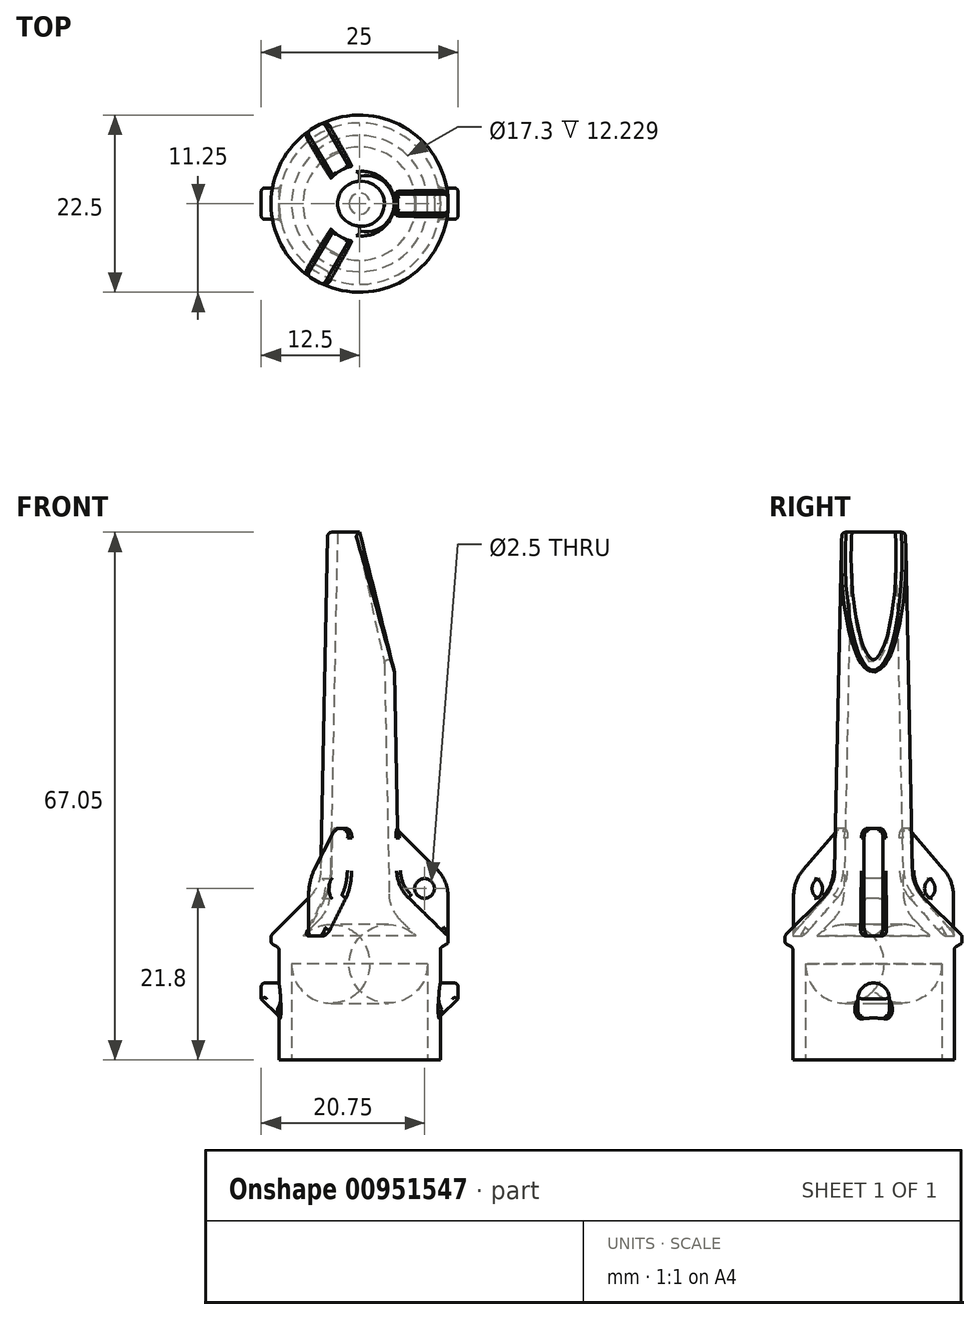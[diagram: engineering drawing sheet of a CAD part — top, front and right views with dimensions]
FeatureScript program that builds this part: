
annotation { "Feature Type Name" : "Feature", "Feature Type Description" : "" }
export const myFeature = defineFeature(function(context is Context, id is Id, definition is map)
    precondition{}
    {
        {
            var Q0;
            Q0=qCreatedBy(makeId("Front.planeOp"),FACE);
            var sketch = newSketch(context, id + "F0", { "sketchPlane" : qUnion([Q0])});
            skLineSegment(sketch, "E0", {"start": v(0, 0) * mm, "end": v(4.05, 0) * mm});
            skLineSegment(sketch, "E1", {"start": v(4.05, 0) * mm, "end": v(5, 45) * mm});
            skLineSegment(sketch, "E2", {"start": v(5, 45) * mm, "end": v(11.25, 51.25) * mm});
            skLineSegment(sketch, "E3", {"start": v(11.25, 51.25) * mm, "end": v(11.25, 52.75) * mm});
            skLineSegment(sketch, "E4", {"start": v(11.25, 52.75) * mm, "end": v(10.25, 52.75) * mm});
            skLineSegment(sketch, "E5", {"start": v(10.25, 52.75) * mm, "end": v(10.25, 67.05) * mm});
            skLineSegment(sketch, "E6", {"start": v(10.25, 67.05) * mm, "end": v(0, 67.05) * mm});
            skLineSegment(sketch, "E7", {"start": v(0, 67.05) * mm, "end": v(0, 0) * mm});
            skSolve(sketch);
        }
        {
            var Q0;
            Q0=qCreatedBy(makeId("Front.planeOp"),FACE);
            var sketch = newSketch(context, id + "F1", { "sketchPlane" : qUnion([Q0])});
            skLineSegment(sketch, "E8", {"start": v(0, 67.05) * mm, "end": v(8.65, 67.05) * mm});
            skLineSegment(sketch, "E9", {"start": v(8.65, 67.05) * mm, "end": v(8.65, 52.75) * mm});
            skLineSegment(sketch, "E10", {"start": v(8.65, 52.75) * mm, "end": v(3.81, 47.91) * mm});
            skLineSegment(sketch, "E11", {"start": v(3.81, 47.91) * mm, "end": v(2.8, 0) * mm});
            skLineSegment(sketch, "E12", {"start": v(2.8, 0) * mm, "end": v(0, 0) * mm});
            skLineSegment(sketch, "E13", {"start": v(0, 0) * mm, "end": v(0, 67.05) * mm});
            skSolve(sketch);
        }
        {
            var Q0;
            Q0=qSketchRegion(id+"F0",true);
            var Q1;
            Q1=sQuery(id+"F0.wireOp",EDGE,"E7");
            revolve(context, id + "F2", {"surfaceOperationType" : NewSurfaceOperationType.NEW, "entities" : qUnion([Q0]), "axis" : qUnion([Q1]), "revolveType" : RevolveType.FULL});
        }
        {
            var Q0;
            Q0=makeQuery(id+"F2.opRevolve","SWEPT_EDGE",EDGE,{"disambiguationData":[OSD([sQuery(id+"F0.wireOp",EDGE,"E1"),sQuery(id+"F0.wireOp",EDGE,"E2")])]});
            fillet(context, id + "F3", {"entities" : qUnion([Q0]), "radius" : 5 * mm, "tangentPropagation" : true, "allowEdgeOverflow" : false});
        }
        {
            var Q0;
            Q0=makeQuery(id+"F2.opRevolve","SWEPT_EDGE",EDGE,{"disambiguationData":[OSD([sQuery(id+"F0.wireOp",EDGE,"E2"),sQuery(id+"F0.wireOp",EDGE,"E3")])]});
            fillet(context, id + "F4", {"entities" : qUnion([Q0]), "radius" : 0.5 * mm, "tangentPropagation" : true, "allowEdgeOverflow" : false});
        }
        {
            var Q0;
            Q0=qCreatedBy(makeId("Front.planeOp"),FACE);
            var sketch = newSketch(context, id + "F5", { "sketchPlane" : qUnion([Q0])});
            skLineSegment(sketch, "E14", {"start": v(0, 51.25) * mm, "end": v(11.25, 51.25) * mm});
            skLineSegment(sketch, "E15", {"start": v(11.25, 51.25) * mm, "end": v(11.25, 44.25) * mm});
            skLineSegment(sketch, "E16", {"start": v(11.25, 44.25) * mm, "end": v(0, 33) * mm});
            skLineSegment(sketch, "E17", {"start": v(0, 33) * mm, "end": v(0, 51.25) * mm});
            skLineSegment(sketch, "E18", {"start": v(8.25, 44.25) * mm, "end": v(11.25, 44.25) * mm, "construction": true});
            skLineSegment(sketch, "E19", {"start": v(8.25, 44.25) * mm, "end": v(8.25, 45.25) * mm, "construction": true});
            skCircle(sketch, "E20", {"center": v(8.25, 45.25) * mm, "radius": 1.25 * mm});
            skSolve(sketch);
        }
        {
            var Q0;
            Q0=qSketchRegion(id+"F5",true);
            extrude(context, id + "F6", {"entities" : qUnion([Q0]), "endBound" : BoundingType.SYMMETRIC, "depth" : 2.4 * mm, "offsetDistance" : 25 * mm});
        }
        {
            var Q0;
            Q0=makeQuery(id+"F6.opExtrude","SWEPT_EDGE",EDGE,{"disambiguationData":[OSD([sQuery(id+"F5.wireOp",EDGE,"E15"),sQuery(id+"F5.wireOp",EDGE,"E16")])]});
            fillet(context, id + "F7", {"entities" : qUnion([Q0]), "radius" : 5 * mm, "tangentPropagation" : true, "allowEdgeOverflow" : false});
        }
        {
            var Q0;
            Q0=makeQuery(id+"F6.opExtrude","CAP_EDGE",EDGE,{"disambiguationData":[OSD([sQuery(id+"F5.wireOp",EDGE,"E15")])],"isStart":false});
            var Q1;
            {var subQ0=sQuery(id+"F5.wireOp",EDGE,"E16");var subQ1=sQuery(id+"F5.wireOp",EDGE,"E15");Q1=makeQuery(id+"F7.opFillet","BLEND_EDGE",EDGE,{"blendedFrom":[makeQuery(id+"F6.opExtrude","SWEPT_EDGE",EDGE,{"disambiguationData":[OSD([subQ1,subQ0])]}),makeQuery(id+"F6.opExtrude","CAP_FACE",FACE,{"disambiguationData":[OSD([sQuery(id+"F5.wireOp",EDGE,"E14"),subQ1,subQ0,sQuery(id+"F5.wireOp",EDGE,"E17")])],"isStart":true})],"blendedInto":[makeQuery(id+"F6.opExtrude","CAP_FACE",FACE,{"disambiguationData":[OSD([sQuery(id+"F5.wireOp",EDGE,"E14"),subQ1,subQ0,sQuery(id+"F5.wireOp",EDGE,"E17")])],"isStart":true})]});}
            fillet(context, id + "F8", {"entities" : qUnion([Q0, Q1]), "radius" : 0.5 * mm, "tangentPropagation" : true, "allowEdgeOverflow" : false});
        }
        {
            var Q0;
            Q0=makeQuery(id+"F6.opExtrude","SWEPT_BODY",BODY,{"disambiguationData":[OSD([sQuery(id+"F5.wireOp",EDGE,"E14"),sQuery(id+"F5.wireOp",EDGE,"E15"),sQuery(id+"F5.wireOp",EDGE,"E16"),sQuery(id+"F5.wireOp",EDGE,"E17")])]});
            var Q1;
            Q1=sQuery(id+"F0.wireOp",EDGE,"E7");
            circularPattern(context, id + "F9", {"operationType" : NewBodyOperationType.ADD, "entities" : qUnion([Q0]), "axis" : qUnion([Q1]), "angle" : 240 * degree, "instanceCount" : 3, "equalSpace" : true});
        }
        {
            var Q0;
            Q0=makeQuery(id+"F9.boolean.opBoolean","INTERSECT",EDGE,{"derivedFrom":[makeQuery(id+"F2.opRevolve","SWEPT_FACE",FACE,{"disambiguationData":[OSD([sQuery(id+"F0.wireOp",EDGE,"E2")])]}),makeQuery(id+"F9.opPattern","COPY",FACE,{"derivedFrom":makeQuery(id+"F6.opExtrude","CAP_FACE",FACE,{"disambiguationData":[OSD([sQuery(id+"F5.wireOp",EDGE,"E14"),sQuery(id+"F5.wireOp",EDGE,"E15"),sQuery(id+"F5.wireOp",EDGE,"E16"),sQuery(id+"F5.wireOp",EDGE,"E17")])],"isStart":false}),"instanceName":"1"})]});
            var Q1;
            Q1=makeQuery(id+"F9.boolean.opBoolean","INTERSECT",EDGE,{"derivedFrom":[makeQuery(id+"F2.opRevolve","SWEPT_FACE",FACE,{"disambiguationData":[OSD([sQuery(id+"F0.wireOp",EDGE,"E2")])]}),makeQuery(id+"F9.opPattern","COPY",FACE,{"derivedFrom":makeQuery(id+"F6.opExtrude","CAP_FACE",FACE,{"disambiguationData":[OSD([sQuery(id+"F5.wireOp",EDGE,"E14"),sQuery(id+"F5.wireOp",EDGE,"E15"),sQuery(id+"F5.wireOp",EDGE,"E16"),sQuery(id+"F5.wireOp",EDGE,"E17")])],"isStart":true}),"instanceName":"2"})]});
            var Q2;
            Q2=makeQuery(id+"F9.boolean.opBoolean","INTERSECT",EDGE,{"derivedFrom":[makeQuery(id+"F2.opRevolve","SWEPT_FACE",FACE,{"disambiguationData":[OSD([sQuery(id+"F0.wireOp",EDGE,"E2")])]}),makeQuery(id+"F6.opExtrude","CAP_FACE",FACE,{"disambiguationData":[OSD([sQuery(id+"F5.wireOp",EDGE,"E14"),sQuery(id+"F5.wireOp",EDGE,"E15"),sQuery(id+"F5.wireOp",EDGE,"E16"),sQuery(id+"F5.wireOp",EDGE,"E17")])],"isStart":false})]});
            var Q3;
            Q3=makeQuery(id+"F6.opExtrude","CAP_EDGE",EDGE,{"disambiguationData":[OSD([sQuery(id+"F5.wireOp",EDGE,"E20")])],"isStart":false});
            var Q4;
            Q4=makeQuery(id+"F6.opExtrude","CAP_EDGE",EDGE,{"disambiguationData":[OSD([sQuery(id+"F5.wireOp",EDGE,"E20")])],"isStart":true});
            var Q5;
            Q5=makeQuery(id+"F9.opPattern","COPY",EDGE,{"derivedFrom":makeQuery(id+"F6.opExtrude","CAP_EDGE",EDGE,{"disambiguationData":[OSD([sQuery(id+"F5.wireOp",EDGE,"E20")])],"isStart":true}),"instanceName":"1"});
            var Q6;
            Q6=makeQuery(id+"F9.opPattern","COPY",EDGE,{"derivedFrom":makeQuery(id+"F6.opExtrude","CAP_EDGE",EDGE,{"disambiguationData":[OSD([sQuery(id+"F5.wireOp",EDGE,"E20")])],"isStart":false}),"instanceName":"2"});
            var Q7;
            Q7=makeQuery(id+"F9.opPattern","COPY",EDGE,{"derivedFrom":makeQuery(id+"F6.opExtrude","CAP_EDGE",EDGE,{"disambiguationData":[OSD([sQuery(id+"F5.wireOp",EDGE,"E20")])],"isStart":true}),"instanceName":"2"});
            var Q8;
            Q8=makeQuery(id+"F9.opPattern","COPY",EDGE,{"derivedFrom":makeQuery(id+"F6.opExtrude","CAP_EDGE",EDGE,{"disambiguationData":[OSD([sQuery(id+"F5.wireOp",EDGE,"E20")])],"isStart":false}),"instanceName":"1"});
            fillet(context, id + "F10", {"entities" : qUnion([Q0, Q1, Q2, Q3, Q4, Q5, Q6, Q7, Q8]), "radius" : 0.5 * mm, "tangentPropagation" : true, "allowEdgeOverflow" : false});
        }
        {
            var Q0;
            Q0=makeQuery(id+"F2.opRevolve","SWEPT_EDGE",EDGE,{"disambiguationData":[OSD([sQuery(id+"F0.wireOp",EDGE,"E3"),sQuery(id+"F0.wireOp",EDGE,"E4")])]});
            chamfer(context, id + "F11", {"entities" : qUnion([Q0]), "chamferType" : ChamferType.TWO_OFFSETS, "width1" : 0.5 * mm, "oppositeDirection" : true, "width2" : 1 * mm, "tangentPropagation" : true});
        }
        {
            var Q0;
            Q0=qCreatedBy(makeId("Front.planeOp"),FACE);
            var sketch = newSketch(context, id + "F12", { "sketchPlane" : qUnion([Q0])});
            skLineSegment(sketch, "E21", {"start": v(0, 57.25) * mm, "end": v(12.5, 57.25) * mm});
            skLineSegment(sketch, "E22", {"start": v(12.5, 57.25) * mm, "end": v(12.5, 59.25) * mm});
            skLineSegment(sketch, "E23", {"start": v(12.5, 59.25) * mm, "end": v(6.5, 65.25) * mm});
            skLineSegment(sketch, "E24", {"start": v(6.5, 65.25) * mm, "end": v(0, 65.25) * mm});
            skLineSegment(sketch, "E25", {"start": v(0, 65.25) * mm, "end": v(0, 57.25) * mm});
            skSolve(sketch);
        }
        {
            var Q0;
            Q0 = qSketchRegion(id + "F12", true);
            extrude(context, id + "F13", {"entities" : qUnion([Q0]), "endBound" : BoundingType.SYMMETRIC, "depth" : 4 * mm, "offsetDistance" : 25 * mm});
        }
        {
            var Q0;
            Q0=makeQuery(id+"F13.opExtrude","CAP_EDGE",EDGE,{"disambiguationData":[OSD([sQuery(id+"F12.wireOp",EDGE,"E21")])],"isStart":false});
            var Q1;
            Q1=makeQuery(id+"F13.opExtrude","CAP_EDGE",EDGE,{"disambiguationData":[OSD([sQuery(id+"F12.wireOp",EDGE,"E21")])],"isStart":true});
            fillet(context, id + "F14", {"entities" : qUnion([Q0, Q1]), "radius" : 2 * mm, "tangentPropagation" : true, "allowEdgeOverflow" : false});
        }
        {
            var Q0;
            Q0=makeQuery(id+"F13.opExtrude","SWEPT_BODY",BODY,{"disambiguationData":[OSD([sQuery(id+"F12.wireOp",EDGE,"E21"),sQuery(id+"F12.wireOp",EDGE,"E22"),sQuery(id+"F12.wireOp",EDGE,"E23"),sQuery(id+"F12.wireOp",EDGE,"E24"),sQuery(id+"F12.wireOp",EDGE,"E25")])]});
            var Q1;
            Q1=sQuery(id+"F1.wireOp",EDGE,"E13");
            circularPattern(context, id + "F15", {"operationType" : NewBodyOperationType.ADD, "entities" : qUnion([Q0]), "axis" : qUnion([Q1]), "angle" : 360 * degree, "instanceCount" : 2, "equalSpace" : true});
        }
        {
            var Q0;
            Q0=makeQuery(id+"F13.opExtrude","CAP_EDGE",EDGE,{"disambiguationData":[OSD([sQuery(id+"F12.wireOp",EDGE,"E23")])],"isStart":true});
            var Q1;
            Q1=makeQuery(id+"F13.opExtrude","CAP_EDGE",EDGE,{"disambiguationData":[OSD([sQuery(id+"F12.wireOp",EDGE,"E23")])],"isStart":false});
            var Q2;
            Q2=makeQuery(id+"F14.opFillet","BLEND_EDGE",EDGE,{"blendedFrom":[makeQuery(id+"F13.opExtrude","CAP_EDGE",EDGE,{"disambiguationData":[OSD([sQuery(id+"F12.wireOp",EDGE,"E21")])],"isStart":true}),makeQuery(id+"F13.opExtrude","SWEPT_FACE",FACE,{"disambiguationData":[OSD([sQuery(id+"F12.wireOp",EDGE,"E22")])]})],"blendedInto":[makeQuery(id+"F13.opExtrude","SWEPT_FACE",FACE,{"disambiguationData":[OSD([sQuery(id+"F12.wireOp",EDGE,"E22")])]})]});
            var Q3;
            Q3=makeQuery(id+"F15.boolean.opBoolean","INTERSECT",EDGE,{"derivedFrom":[makeQuery(id+"F2.opRevolve","SWEPT_FACE",FACE,{"disambiguationData":[OSD([sQuery(id+"F0.wireOp",EDGE,"E5")])]}),makeQuery(id+"F13.opExtrude","SWEPT_FACE",FACE,{"disambiguationData":[OSD([sQuery(id+"F12.wireOp",EDGE,"E23")])]})]});
            var Q4;
            Q4=makeQuery(id+"F15.opPattern","COPY",EDGE,{"derivedFrom":makeQuery(id+"F13.opExtrude","CAP_EDGE",EDGE,{"disambiguationData":[OSD([sQuery(id+"F12.wireOp",EDGE,"E23")])],"isStart":false}),"instanceName":"1"});
            var Q5;
            Q5=makeQuery(id+"F15.opPattern","COPY",EDGE,{"derivedFrom":makeQuery(id+"F13.opExtrude","CAP_EDGE",EDGE,{"disambiguationData":[OSD([sQuery(id+"F12.wireOp",EDGE,"E23")])],"isStart":true}),"instanceName":"1"});
            var Q6;
            Q6=makeQuery(id+"F15.boolean.opBoolean","INTERSECT",EDGE,{"derivedFrom":[makeQuery(id+"F2.opRevolve","SWEPT_FACE",FACE,{"disambiguationData":[OSD([sQuery(id+"F0.wireOp",EDGE,"E5")])]}),makeQuery(id+"F15.opPattern","COPY",FACE,{"derivedFrom":makeQuery(id+"F13.opExtrude","SWEPT_FACE",FACE,{"disambiguationData":[OSD([sQuery(id+"F12.wireOp",EDGE,"E23")])]}),"instanceName":"1"})]});
            var Q7;
            Q7=makeQuery(id+"F15.opPattern","COPY",EDGE,{"derivedFrom":makeQuery(id+"F14.opFillet","BLEND_EDGE",EDGE,{"blendedFrom":[makeQuery(id+"F13.opExtrude","CAP_EDGE",EDGE,{"disambiguationData":[OSD([sQuery(id+"F12.wireOp",EDGE,"E21")])],"isStart":true}),makeQuery(id+"F13.opExtrude","SWEPT_FACE",FACE,{"disambiguationData":[OSD([sQuery(id+"F12.wireOp",EDGE,"E22")])]})],"blendedInto":[makeQuery(id+"F13.opExtrude","SWEPT_FACE",FACE,{"disambiguationData":[OSD([sQuery(id+"F12.wireOp",EDGE,"E22")])]})]}),"instanceName":"1"});
            fillet(context, id + "F16", {"entities" : qUnion([Q0, Q1, Q2, Q3, Q4, Q5, Q6, Q7]), "radius" : 0.5 * mm, "tangentPropagation" : true, "allowEdgeOverflow" : false});
        }
        {
            var Q0;
            Q0=qSketchRegion(id+"F1",true);
            var Q1;
            Q1=sQuery(id+"F1.wireOp",EDGE,"E13");
            revolve(context, id + "F17", {"operationType" : NewBodyOperationType.REMOVE, "surfaceOperationType" : NewSurfaceOperationType.NEW, "entities" : qUnion([Q0]), "axis" : qUnion([Q1]), "revolveType" : RevolveType.FULL, "oppositeDirection" : true});
        }
        {
            var Q0;
            Q0=makeQuery(id+"F17.boolean.opBoolean","COPY",EDGE,{"derivedFrom":makeQuery(id+"F17.opRevolve","SWEPT_EDGE",EDGE,{"disambiguationData":[OSD([sQuery(id+"F1.wireOp",EDGE,"E10"),sQuery(id+"F1.wireOp",EDGE,"E11")])]})});
            var Q1;
            Q1=makeQuery(id+"F17.boolean.opBoolean","COPY",EDGE,{"derivedFrom":makeQuery(id+"F17.opRevolve","SWEPT_EDGE",EDGE,{"disambiguationData":[OSD([sQuery(id+"F1.wireOp",EDGE,"E9"),sQuery(id+"F1.wireOp",EDGE,"E10")])]})});
            fillet(context, id + "F18", {"entities" : qUnion([Q0, Q1]), "radius" : 5 * mm, "tangentPropagation" : true, "allowEdgeOverflow" : false});
        }
        {
            var Q0;
            {var subQ0=sQuery(id+"F0.wireOp",EDGE,"E3");Q0=makeQuery(id+"F11.opChamfer","BLEND_EDGE",EDGE,{"blendedFrom":[makeQuery(id+"F2.opRevolve","SWEPT_EDGE",EDGE,{"disambiguationData":[OSD([subQ0,sQuery(id+"F0.wireOp",EDGE,"E4")])]}),makeQuery(id+"F2.opRevolve","SWEPT_FACE",FACE,{"disambiguationData":[OSD([subQ0])]})],"blendedInto":[makeQuery(id+"F2.opRevolve","SWEPT_FACE",FACE,{"disambiguationData":[OSD([subQ0])]})]});}
            var Q1;
            Q1=makeQuery(id+"F11.opChamfer","BLEND_EDGE",EDGE,{"blendedFrom":[makeQuery(id+"F2.opRevolve","SWEPT_EDGE",EDGE,{"disambiguationData":[OSD([sQuery(id+"F0.wireOp",EDGE,"E3"),sQuery(id+"F0.wireOp",EDGE,"E4")])]}),makeQuery(id+"F2.opRevolve","SWEPT_FACE",FACE,{"disambiguationData":[OSD([sQuery(id+"F0.wireOp",EDGE,"E5")])]})],"blendedInto":[makeQuery(id+"F2.opRevolve","SWEPT_FACE",FACE,{"disambiguationData":[OSD([sQuery(id+"F0.wireOp",EDGE,"E5")])]})]});
            fillet(context, id + "F19", {"entities" : qUnion([Q0, Q1]), "radius" : 0.5 * mm, "tangentPropagation" : true, "allowEdgeOverflow" : false});
        }
        {
            var Q0;
            Q0=qCreatedBy(makeId("Front.planeOp"),FACE);
            var sketch = newSketch(context, id + "F20", { "sketchPlane" : qUnion([Q0])});
            skLineSegment(sketch, "E26", {"start": v(0, 0) * mm, "end": v(5, 20) * mm});
            skLineSegment(sketch, "E27", {"start": v(5, 20) * mm, "end": v(5, 0) * mm});
            skLineSegment(sketch, "E28", {"start": v(5, 0) * mm, "end": v(0, 0) * mm});
            skSolve(sketch);
        }
        {
            var Q0;
            Q0 = qSketchRegion(id + "F20", true);
            extrude(context, id + "F21", {"entities" : qUnion([Q0]), "operationType" : NewBodyOperationType.REMOVE, "endBound" : BoundingType.SYMMETRIC, "oppositeDirection" : true, "depth" : 25 * mm, "offsetDistance" : 25 * mm});
        }
        {
            var Q0;
            Q0=makeQuery(id+"F2.opRevolve","SWEPT_EDGE",EDGE,{"disambiguationData":[OSD([sQuery(id+"F0.wireOp",EDGE,"E0"),sQuery(id+"F0.wireOp",EDGE,"E1")])]});
            var Q1;
            Q1=makeQuery(id+"F21.boolean.opBoolean","COPY",EDGE,{"disambiguationData":[OD(0.0)],"derivedFrom":makeQuery(id+"F21.opExtrude","SWEPT_EDGE",EDGE,{"disambiguationData":[OSD([sQuery(id+"F20.wireOp",EDGE,"E26"),sQuery(id+"F20.wireOp",EDGE,"E28")])]})});
            var Q2;
            Q2=makeQuery(id+"F21.boolean.opBoolean","COPY",EDGE,{"disambiguationData":[OD(1.0)],"derivedFrom":makeQuery(id+"F21.opExtrude","SWEPT_EDGE",EDGE,{"disambiguationData":[OSD([sQuery(id+"F20.wireOp",EDGE,"E26"),sQuery(id+"F20.wireOp",EDGE,"E28")])]})});
            var Q3;
            Q3=makeQuery(id+"F21.boolean.opBoolean","INTERSECT",EDGE,{"derivedFrom":[makeQuery(id+"F2.opRevolve","SWEPT_FACE",FACE,{"disambiguationData":[OSD([sQuery(id+"F0.wireOp",EDGE,"E1")])]}),makeQuery(id+"F21.opExtrude","SWEPT_FACE",FACE,{"disambiguationData":[OSD([sQuery(id+"F20.wireOp",EDGE,"E26")])]})]});
            var Q4;
            Q4=makeQuery(id+"F21.boolean.opBoolean","INTERSECT",EDGE,{"derivedFrom":[makeQuery(id+"F17.boolean.opBoolean","COPY",FACE,{"derivedFrom":makeQuery(id+"F17.opRevolve","SWEPT_FACE",FACE,{"disambiguationData":[OSD([sQuery(id+"F1.wireOp",EDGE,"E11")])]})}),makeQuery(id+"F21.opExtrude","SWEPT_FACE",FACE,{"disambiguationData":[OSD([sQuery(id+"F20.wireOp",EDGE,"E26")])]})]});
            var Q5;
            Q5=makeQuery(id+"F17.boolean.opBoolean","COPY",EDGE,{"derivedFrom":makeQuery(id+"F17.opRevolve","SWEPT_EDGE",EDGE,{"disambiguationData":[OSD([sQuery(id+"F1.wireOp",EDGE,"E11"),sQuery(id+"F1.wireOp",EDGE,"E12")])]})});
            fillet(context, id + "F22", {"entities" : qUnion([Q0, Q1, Q2, Q3, Q4, Q5]), "radius" : 0.5 * mm, "tangentPropagation" : true, "allowEdgeOverflow" : false});
        }
        {
            var Q0;
            Q0=makeQuery(id+"F2.opRevolve","SWEPT_BODY",BODY,{"disambiguationData":[OSD([sQuery(id+"F0.wireOp",EDGE,"E0"),sQuery(id+"F0.wireOp",EDGE,"E1"),sQuery(id+"F0.wireOp",EDGE,"E2"),sQuery(id+"F0.wireOp",EDGE,"E3"),sQuery(id+"F0.wireOp",EDGE,"E4"),sQuery(id+"F0.wireOp",EDGE,"E5"),sQuery(id+"F0.wireOp",EDGE,"E6"),sQuery(id+"F0.wireOp",EDGE,"E7")])]});
            var Q1;
            Q1=sQuery(id+"F5.wireOp",EDGE,"E14");
            transform(context, id + "F23", {"entities" : qUnion([Q0]), "transformType" : TransformType.ROTATION, "transformAxis" : qUnion([Q1]), "angle" : 180 * degree, "makeCopy" : false});
        }
    });
